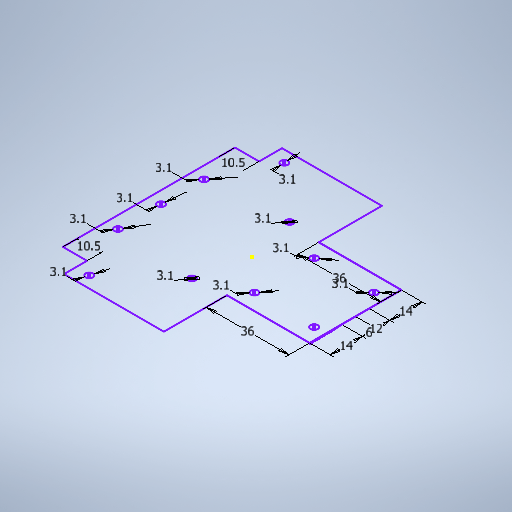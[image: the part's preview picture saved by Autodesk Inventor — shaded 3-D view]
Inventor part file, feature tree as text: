
AUTODESK INVENTOR PART (.ipt)
format: ipt  version: 2025 (Build 290162000, 162)  size: 275,968 bytes
history: native  units: in
note: dims shown in document units (in); Inventor stores cm internally (conversion verified against a paired STEP export)
features: sketch x1
ambient origin geometry x8: Origin, YZ Plane, XZ Plane, XY Plane, X Axis, Y Axis, Z Axis, Center Point
feature tree (1):
  sketch  "Sketch1"  dims[d2=0.2362in d3=0.4724in d4=0.5512in d5=0.5512in d6=1.4173in d7=1.4173in d13=0.122in d14=0.122in d15=0.122in d17=0.4134in d19=0.4134in d22=0.122in d23=0.122in d27=0.122in d28=0.122in d32=0.122in d33=0.122in d34=0.122in]
